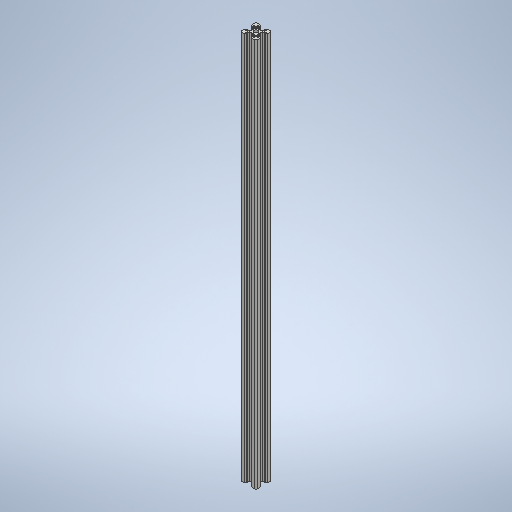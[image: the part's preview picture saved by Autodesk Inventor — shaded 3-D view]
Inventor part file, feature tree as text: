
AUTODESK INVENTOR PART (.ipt)
format: ipt  version: 2025.2 (Build 292293000, 293)  size: 411,136 bytes
history: native  units: mm
features: other x1, extrude x1, sketch x1
ambient origin geometry x8: Origin, YZ Plane, XZ Plane, XY Plane, X Axis, Y Axis, Z Axis, Center Point
bodies: Body1 (feature_tree)
feature tree (3):
  other  "Твердое тело1"
  extrude  "Выдавливание1"  Depth=0.25mm
  sketch  "Эскиз1"
